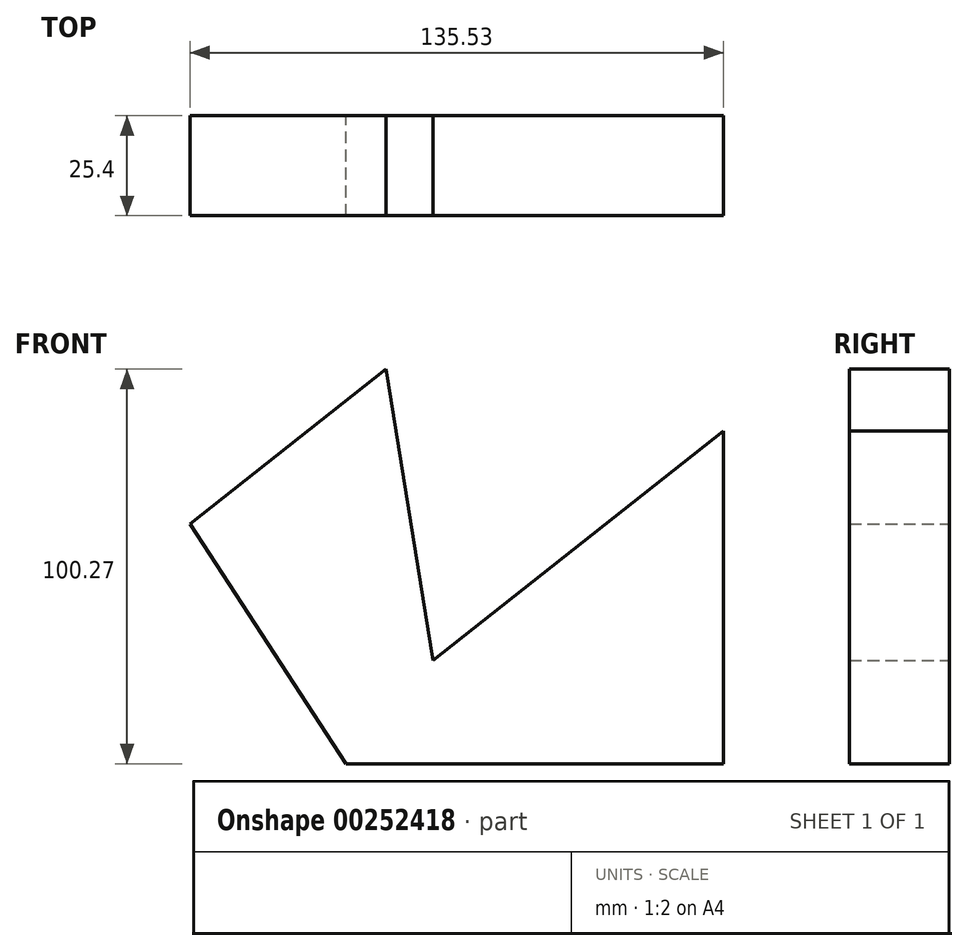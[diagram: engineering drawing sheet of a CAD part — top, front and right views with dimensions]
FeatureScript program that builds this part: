
annotation { "Feature Type Name" : "Feature", "Feature Type Description" : "" }
export const myFeature = defineFeature(function(context is Context, id is Id, definition is map)
    precondition{}
    {
        {
            var Q0;
            Q0=qCreatedBy(makeId("Front.planeOp"),FACE);
            var sketch = newSketch(context, id + "F0", { "sketchPlane" : qUnion([Q0])});
            skLineSegment(sketch, "E0", {"start": v(-67.91, 13.26) * mm, "end": v(-28.27, -47.66) * mm});
            skLineSegment(sketch, "E1", {"start": v(-28.27, -47.66) * mm, "end": v(67.62, -47.66) * mm});
            skLineSegment(sketch, "E2", {"start": v(67.62, -47.66) * mm, "end": v(67.62, 36.87) * mm});
            skLineSegment(sketch, "E3", {"start": v(67.62, 36.87) * mm, "end": v(-6.12, -21.42) * mm});
            skLineSegment(sketch, "E4", {"start": v(-6.12, -21.42) * mm, "end": v(-18.07, 52.61) * mm});
            skLineSegment(sketch, "E5", {"start": v(-67.91, 13.26) * mm, "end": v(-18.07, 52.61) * mm});
            skSolve(sketch);
        }
        {
            var Q0;
            Q0 = qSketchRegion(id + "F0", true);
            extrude(context, id + "F1", {"entities" : qUnion([Q0]), "endBound" : BoundingType.SYMMETRIC, "depth" : 25.4 * mm});
        }
    });
